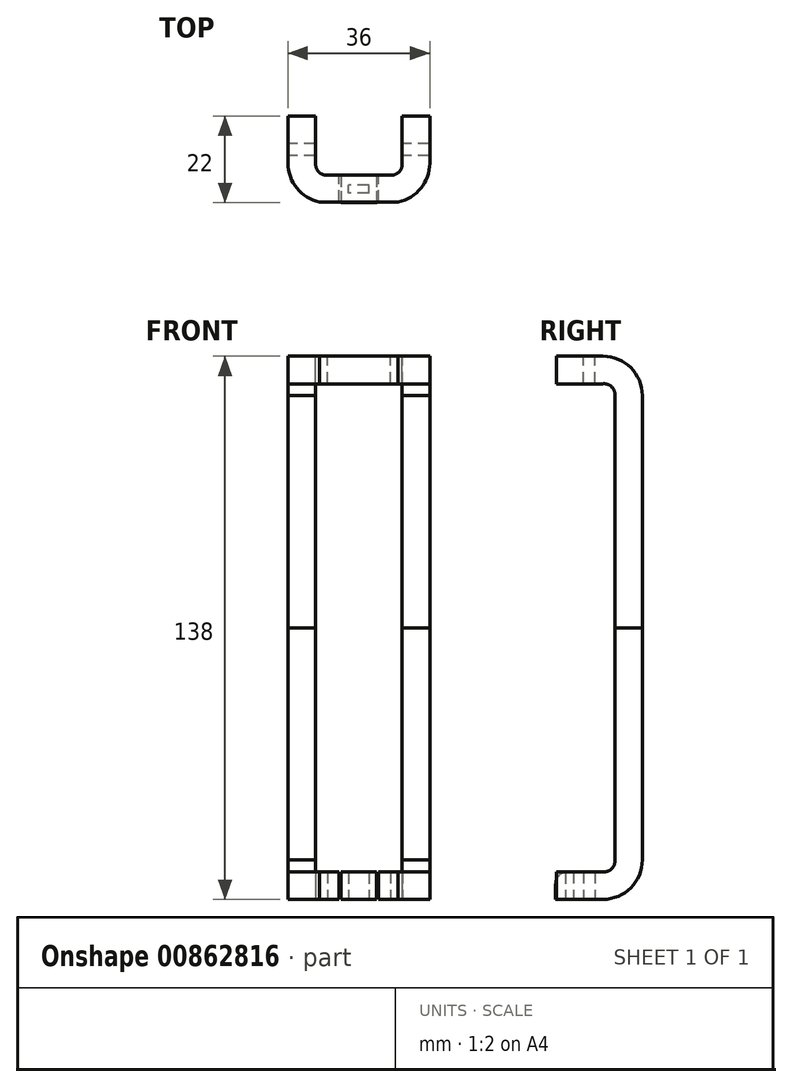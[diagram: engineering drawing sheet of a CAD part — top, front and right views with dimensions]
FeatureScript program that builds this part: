
annotation { "Feature Type Name" : "Feature", "Feature Type Description" : "" }
export const myFeature = defineFeature(function(context is Context, id is Id, definition is map)
    precondition{}
    {
        {
            assignVariable(context, id + "F0", {"name" : "frame_width", "anyValue" : 7});
        }
        {
            assignVariable(context, id + "F1", {"name" : "phone_height", "anyValue" : 138});
        }
        {
            var Q0;
            Q0=qCreatedBy(makeId("Top.planeOp"),FACE);
            var sketch = newSketch(context, id + "F2", { "sketchPlane" : qUnion([Q0])});
            skLineSegment(sketch, "E0", {"start": v(-126.35, 500.54) * mm, "end": v(-119.35, 500.54) * mm, "construction": true});
            skLineSegment(sketch, "E1", {"start": v(-126.35, 500.54) * mm, "end": v(-126.35, 495.54) * mm});
            skLineSegment(sketch, "E2", {"start": v(-116.35, 485.54) * mm, "end": v(-113.35, 485.54) * mm});
            skLineSegment(sketch, "E3", {"start": v(-113.35, 485.54) * mm, "end": v(-108.35, 485.54) * mm, "construction": true});
            skPoint(sketch, "E4.visualSharp", {"position": v(-126.35, 485.54) * mm});
            skArc(sketch, "E4.filletArc", {"start": v(-126.35, 495.54) * mm, "mid": v(-123.42, 488.47) * mm, "end": v(-116.35, 485.54) * mm});
            skPoint(sketch, "E5.visualSharp", {"position": v(-65.23, 485.8) * mm});
            skLineSegment(sketch, "E6", {"start": v(-113.35, 485.54) * mm, "end": v(-113.35, 492.54) * mm});
            skLineSegment(sketch, "E7", {"start": v(-126.35, 495.54) * mm, "end": v(-119.35, 495.54) * mm, "construction": true});
            skLineSegment(sketch, "E8", {"start": v(-116.35, 485.54) * mm, "end": v(-116.35, 492.54) * mm, "construction": true});
            skArc(sketch, "E9", {"start": v(-119.35, 495.54) * mm, "mid": v(-118.53, 493.36) * mm, "end": v(-116.35, 492.54) * mm});
            skLineSegment(sketch, "E10", {"start": v(-116.35, 492.54) * mm, "end": v(-113.35, 492.54) * mm});
            skLineSegment(sketch, "E11", {"start": v(-119.35, 495.54) * mm, "end": v(-119.35, 500.54) * mm});
            skLineSegment(sketch, "E12", {"start": v(-113.35, 489.04) * mm, "end": v(-108.35, 489.04) * mm, "construction": true});
            skLineSegment(sketch, "E13", {"start": v(-108.35, 489.04) * mm, "end": v(-103.35, 489.04) * mm, "construction": true});
            skLineSegment(sketch, "E14", {"start": v(-108.35, 489.04) * mm, "end": v(-108.35, 479.6) * mm, "construction": true});
            skLineSegment(sketch, "E15", {"start": v(-108.35, 489.04) * mm, "end": v(-108.35, 497.32) * mm, "construction": true});
            skLineSegment(sketch, "E16.MirrorCS", {"start": v(-103.35, 485.54) * mm, "end": v(-108.35, 485.54) * mm, "construction": true});
            skLineSegment(sketch, "E17.MirrorCS", {"start": v(-103.35, 485.54) * mm, "end": v(-103.35, 492.54) * mm});
            skLineSegment(sketch, "E18.MirrorCS", {"start": v(-100.35, 485.54) * mm, "end": v(-103.35, 485.54) * mm});
            skLineSegment(sketch, "E19.MirrorCS", {"start": v(-100.35, 492.54) * mm, "end": v(-103.35, 492.54) * mm});
            skArc(sketch, "E20.MirrorCS", {"start": v(-97.35, 495.54) * mm, "mid": v(-98.16, 493.36) * mm, "end": v(-100.35, 492.54) * mm});
            skArc(sketch, "E21.MirrorCS", {"start": v(-90.35, 495.54) * mm, "mid": v(-93.28, 488.47) * mm, "end": v(-100.35, 485.54) * mm});
            skLineSegment(sketch, "E22.MirrorCS", {"start": v(-90.35, 495.54) * mm, "end": v(-97.35, 495.54) * mm, "construction": true});
            skLineSegment(sketch, "E23.MirrorCS", {"start": v(-97.35, 495.54) * mm, "end": v(-97.35, 500.54) * mm});
            skLineSegment(sketch, "E24.MirrorCS", {"start": v(-90.35, 500.54) * mm, "end": v(-97.35, 500.54) * mm, "construction": true});
            skLineSegment(sketch, "E25.MirrorCS", {"start": v(-90.35, 500.54) * mm, "end": v(-90.35, 495.54) * mm});
            skLineSegment(sketch, "E26", {"start": v(-119.35, 500.54) * mm, "end": v(-119.35, 507.54) * mm});
            skLineSegment(sketch, "E27", {"start": v(-126.35, 500.54) * mm, "end": v(-126.35, 507.54) * mm});
            skLineSegment(sketch, "E28", {"start": v(-126.35, 507.54) * mm, "end": v(-119.35, 507.54) * mm});
            skLineSegment(sketch, "E29.MirrorCS", {"start": v(-97.35, 500.54) * mm, "end": v(-97.35, 507.54) * mm});
            skLineSegment(sketch, "E30.MirrorCS", {"start": v(-90.35, 500.54) * mm, "end": v(-90.35, 507.54) * mm});
            skLineSegment(sketch, "E31.MirrorCS", {"start": v(-90.35, 507.54) * mm, "end": v(-97.35, 507.54) * mm});
            skLineSegment(sketch, "E32", {"start": v(-112.85, 492.54) * mm, "end": v(-112.85, 485.54) * mm, "construction": true});
            skLineSegment(sketch, "E33", {"start": v(-103.85, 492.54) * mm, "end": v(-103.85, 485.54) * mm, "construction": true});
            skLineSegment(sketch, "E34", {"start": v(-113.35, 492.54) * mm, "end": v(-112.85, 492.54) * mm, "construction": true});
            skLineSegment(sketch, "E35", {"start": v(-99.12, 492.54) * mm, "end": v(-112.85, 492.54) * mm, "construction": true});
            skLineSegment(sketch, "E36", {"start": v(-103.35, 492.54) * mm, "end": v(-103.85, 492.54) * mm, "construction": true});
            skLineSegment(sketch, "E37", {"start": v(-103.85, 492.54) * mm, "end": v(-99.12, 492.54) * mm, "construction": true});
            skSolve(sketch);
        }
        {
            var Q0;
            Q0=makeQuery(id+"F2.imprint","IMPRINT",FACE,{"disambiguationData":[TD([[makeQuery(id+"F2.imprint","IMPRINT",EDGE,{"derivedFrom":sQuery(id+"F2.wireOp",EDGE,"E1")}),1.0]])]});
            var Q1;
            Q1=makeQuery(id+"F2.imprint","IMPRINT",FACE,{"disambiguationData":[TD([[makeQuery(id+"F2.imprint","IMPRINT",EDGE,{"derivedFrom":sQuery(id+"F2.wireOp",EDGE,"E17.MirrorCS")}),-1.0]])]});
            extrude(context, id + "F3", {"entities" : qUnion([Q0, Q1]), "depth" : (getVariable(context, 'phone_height')) / 2 * mm, "offsetDistance" : 25 * mm});
        }
        {
            var Q0;
            Q0=makeQuery(id+"F3.opExtrude","SWEPT_FACE",FACE,{"disambiguationData":[OSD([sQuery(id+"F2.wireOp",EDGE,"E1"),sQuery(id+"F2.wireOp",EDGE,"E27")])]});
            var sketch = newSketch(context, id + "F4", { "sketchPlane" : qUnion([Q0])});
            skLineSegment(sketch, "E38", {"start": v(-507.54, 69) * mm, "end": v(-485.74, 69) * mm});
            skLineSegment(sketch, "E39", {"start": v(-485.74, 0) * mm, "end": v(-485.74, 7) * mm});
            skLineSegment(sketch, "E40", {"start": v(-507.54, 10) * mm, "end": v(-507.54, 16.46) * mm});
            skLineSegment(sketch, "E41", {"start": v(-497.54, 0) * mm, "end": v(-485.74, 0) * mm});
            skLineSegment(sketch, "E42", {"start": v(-507.54, 16.46) * mm, "end": v(-507.54, 69) * mm});
            skLineSegment(sketch, "E43", {"start": v(-507.54, 69) * mm, "end": v(-500.57, 69) * mm});
            skLineSegment(sketch, "E44", {"start": v(-500.57, 69) * mm, "end": v(-500.57, 7.1) * mm});
            skLineSegment(sketch, "E45", {"start": v(-507.54, 0) * mm, "end": v(-507.54, 0) * mm});
            skPoint(sketch, "E46", {"position": v(-495.54, 7) * mm});
            skLineSegment(sketch, "E47", {"start": v(-500.54, 7) * mm, "end": v(-500.57, 12) * mm, "construction": true});
            skLineSegment(sketch, "E48", {"start": v(-500.54, 7) * mm, "end": v(-495.54, 7) * mm, "construction": true});
            skLineSegment(sketch, "E49", {"start": v(-485.74, 7) * mm, "end": v(-495.54, 7) * mm});
            skPoint(sketch, "E50.visualSharp", {"position": v(-507.54, 0) * mm});
            skArc(sketch, "E50.filletArc", {"start": v(-507.54, 10) * mm, "mid": v(-504.61, 2.93) * mm, "end": v(-497.54, 0) * mm});
            skPoint(sketch, "E51.endSnap0", {"position": v(-498.04, 7) * mm});
            skLineSegment(sketch, "E52", {"start": v(-507.54, 10) * mm, "end": v(-500.56, 10) * mm});
            skArc(sketch, "E53", {"start": v(-500.56, 10) * mm, "mid": v(-499.76, 7.79) * mm, "end": v(-497.54, 7) * mm});
            skLineSegment(sketch, "E54", {"start": v(-495.54, 7) * mm, "end": v(-497.54, 7) * mm});
            skSolve(sketch);
        }
        {
            var Q0;
            {var subQ8=sQuery(id+"F4.wireOp",EDGE,"E40");Q0=makeQuery(id+"F4.imprint","IMPRINT",FACE,{"disambiguationData":[TD([[makeQuery(id+"F4.imprint","IMPRINT",EDGE,{"derivedFrom":subQ8}),1.0]])]});}
            var Q1;
            {var subQ0=sQuery(id+"F4.wireOp",EDGE,"E39");Q1=makeQuery(id+"F4.imprint","IMPRINT",FACE,{"disambiguationData":[TD([[makeQuery(id+"F4.imprint","IMPRINT",EDGE,{"derivedFrom":subQ0}),1.0]])]});}
            var Q2;
            {var subQ3=sQuery(id+"F4.wireOp",EDGE,"E50.filletArc");Q2=makeQuery(id+"F4.imprint","IMPRINT",FACE,{"disambiguationData":[TD([[makeQuery(id+"F4.imprint","IMPRINT",EDGE,{"derivedFrom":subQ3}),1.0]])]});}
            extrude(context, id + "F5", {"entities" : qUnion([Q0, Q1, Q2]), "operationType" : NewBodyOperationType.INTERSECT, "oppositeDirection" : true, "depth" : 81.7 * mm, "offsetDistance" : 25 * mm});
        }
        {
            var Q0;
            Q0=makeQuery(id+"F3.opExtrude","SWEPT_BODY",BODY,{"disambiguationData":[OSD([sQuery(id+"F2.wireOp",EDGE,"E1"),sQuery(id+"F2.wireOp",EDGE,"E2"),sQuery(id+"F2.wireOp",EDGE,"E3"),sQuery(id+"F2.wireOp",EDGE,"E4.filletArc"),sQuery(id+"F2.wireOp",EDGE,"obsk3g0P-nJtu-QT1G-FohG-gz7rWDq2pBs8"),sQuery(id+"F2.wireOp",EDGE,"E9"),sQuery(id+"F2.wireOp",EDGE,"E10"),sQuery(id+"F2.wireOp",EDGE,"E11"),sQuery(id+"F2.wireOp",EDGE,"f647806e-f1ab-41c5-826c-117e73be01030.MirrorCS"),sQuery(id+"F2.wireOp",EDGE,"E16.MirrorCS"),sQuery(id+"F2.wireOp",EDGE,"E18.MirrorCS"),sQuery(id+"F2.wireOp",EDGE,"E19.MirrorCS"),sQuery(id+"F2.wireOp",EDGE,"E20.MirrorCS"),sQuery(id+"F2.wireOp",EDGE,"E21.MirrorCS"),sQuery(id+"F2.wireOp",EDGE,"E23.MirrorCS"),sQuery(id+"F2.wireOp",EDGE,"E25.MirrorCS"),sQuery(id+"F2.wireOp",EDGE,"E26"),sQuery(id+"F2.wireOp",EDGE,"E27"),sQuery(id+"F2.wireOp",EDGE,"E28"),sQuery(id+"F2.wireOp",EDGE,"E29.MirrorCS"),sQuery(id+"F2.wireOp",EDGE,"E30.MirrorCS"),sQuery(id+"F2.wireOp",EDGE,"E31.MirrorCS")])]});
            var Q1;
            {var subQ0=sQuery(id+"F2.wireOp",EDGE,"E27");var subQ1=sQuery(id+"F2.wireOp",EDGE,"E1");var subQ2=sQuery(id+"F2.wireOp",EDGE,"E26");var subQ3=sQuery(id+"F2.wireOp",EDGE,"E11");var subQ4=sQuery(id+"F2.wireOp",EDGE,"E28");Q1=makeQuery(id+"F5.boolean.opBoolean","SPLIT",FACE,{"disambiguationData":[TD([makeQuery(id+"F3.opExtrude","SWEPT_FACE",FACE,{"disambiguationData":[OSD([subQ4])]})])],"derivedFrom":makeQuery(id+"F3.opExtrude","CAP_FACE",FACE,{"disambiguationData":[OSD([subQ1,sQuery(id+"F2.wireOp",EDGE,"E2"),sQuery(id+"F2.wireOp",EDGE,"E3"),sQuery(id+"F2.wireOp",EDGE,"E4.filletArc"),sQuery(id+"F2.wireOp",EDGE,"obsk3g0P-nJtu-QT1G-FohG-gz7rWDq2pBs8"),sQuery(id+"F2.wireOp",EDGE,"E9"),sQuery(id+"F2.wireOp",EDGE,"E10"),subQ3,sQuery(id+"F2.wireOp",EDGE,"f647806e-f1ab-41c5-826c-117e73be01030.MirrorCS"),sQuery(id+"F2.wireOp",EDGE,"E16.MirrorCS"),sQuery(id+"F2.wireOp",EDGE,"E18.MirrorCS"),sQuery(id+"F2.wireOp",EDGE,"E19.MirrorCS"),sQuery(id+"F2.wireOp",EDGE,"E20.MirrorCS"),sQuery(id+"F2.wireOp",EDGE,"E21.MirrorCS"),sQuery(id+"F2.wireOp",EDGE,"E23.MirrorCS"),sQuery(id+"F2.wireOp",EDGE,"E25.MirrorCS"),subQ2,subQ0,subQ4,sQuery(id+"F2.wireOp",EDGE,"E29.MirrorCS"),sQuery(id+"F2.wireOp",EDGE,"E30.MirrorCS"),sQuery(id+"F2.wireOp",EDGE,"E31.MirrorCS")])],"isStart":false})});}
            mirror(context, id + "F6", {"entities" : qUnion([Q0]), "mirrorPlane" : qUnion([Q1])});
        }
        {
            var Q0;
            Q0=qCreatedBy(makeId("Top.planeOp"),FACE);
            var sketch = newSketch(context, id + "F7", { "sketchPlane" : qUnion([Q0])});
            skLineSegment(sketch, "E55.0", {"start": v(-112.85, 492.54) * mm, "end": v(-112.85, 485.54) * mm, "construction": true});
            skLineSegment(sketch, "E56.0", {"start": v(-99.12, 492.54) * mm, "end": v(-112.85, 492.54) * mm, "construction": true});
            skLineSegment(sketch, "E57.0", {"start": v(-103.85, 492.54) * mm, "end": v(-99.12, 492.54) * mm, "construction": true});
            skLineSegment(sketch, "E58.0", {"start": v(-103.85, 492.54) * mm, "end": v(-103.85, 485.54) * mm, "construction": true});
            skLineSegment(sketch, "E59.0", {"start": v(-103.35, 485.54) * mm, "end": v(-108.35, 485.54) * mm, "construction": true});
            skLineSegment(sketch, "E60.0", {"start": v(-113.35, 485.54) * mm, "end": v(-108.35, 485.54) * mm, "construction": true});
            skLineSegment(sketch, "E61.0", {"start": v(-108.35, 489.04) * mm, "end": v(-108.35, 479.6) * mm, "construction": true});
            skLineSegment(sketch, "E62.0", {"start": v(-108.35, 489.04) * mm, "end": v(-103.35, 489.04) * mm, "construction": true});
            skLineSegment(sketch, "E63.0", {"start": v(-113.35, 489.04) * mm, "end": v(-108.35, 489.04) * mm, "construction": true});
            skLineSegment(sketch, "E64.0", {"start": v(-108.35, 489.04) * mm, "end": v(-108.35, 497.32) * mm, "construction": true});
            skLineSegment(sketch, "E65.bottom", {"start": v(-112.85, 492.54) * mm, "end": v(-103.85, 492.54) * mm});
            skLineSegment(sketch, "E65.top", {"start": v(-112.85, 485.54) * mm, "end": v(-103.85, 485.54) * mm});
            skLineSegment(sketch, "E65.left", {"start": v(-112.85, 492.54) * mm, "end": v(-112.85, 485.54) * mm});
            skLineSegment(sketch, "E65.right", {"start": v(-103.85, 492.54) * mm, "end": v(-103.85, 485.54) * mm});
            skLineSegment(sketch, "E66.bottom", {"start": v(-105.73, 488.05) * mm, "end": v(-110.96, 488.05) * mm});
            skLineSegment(sketch, "E66.top", {"start": v(-105.73, 490.03) * mm, "end": v(-110.96, 490.03) * mm});
            skLineSegment(sketch, "E66.left", {"start": v(-105.73, 488.05) * mm, "end": v(-105.73, 490.03) * mm});
            skLineSegment(sketch, "E66.right", {"start": v(-110.96, 488.05) * mm, "end": v(-110.96, 490.03) * mm});
            skPoint(sketch, "E66.middle", {"position": v(-108.35, 489.04) * mm});
            skSolve(sketch);
        }
        {
            var Q0;
            Q0=makeQuery(id+"F7.imprint","IMPRINT",FACE,{"disambiguationData":[TD([[makeQuery(id+"F7.imprint","IMPRINT",EDGE,{"derivedFrom":sQuery(id+"F7.wireOp",EDGE,"E65.bottom")}),-1.0]])]});
            extrude(context, id + "F8", {"entities" : qUnion([Q0]), "depth" : (getVariable(context, 'frame_width')) * mm, "offsetDistance" : 25 * mm});
        }
        {
            var Q0;
            {var subQ0=sQuery(id+"F4.wireOp",EDGE,"E49");var subQ1=sQuery(id+"F4.wireOp",EDGE,"E39");Q0=makeQuery(id+"F5.boolean.opBoolean","COPY",EDGE,{"disambiguationData":[TD([makeQuery(id+"F3.opExtrude","SWEPT_FACE",FACE,{"disambiguationData":[OSD([sQuery(id+"F2.wireOp",EDGE,"E4.filletArc")])]})])],"derivedFrom":makeQuery(id+"F5.boolean.toolComplement.opBoolean","COPY",EDGE,{"derivedFrom":makeQuery(id+"F5.opExtrude","SWEPT_EDGE",EDGE,{"disambiguationData":[OSD([subQ1,subQ0])]})})});}
            var Q1;
            Q1=makeQuery(id+"F8.opExtrude","CAP_EDGE",EDGE,{"disambiguationData":[OSD([sQuery(id+"F7.wireOp",EDGE,"E65.top")])],"isStart":false});
            var Q2;
            {var subQ0=sQuery(id+"F4.wireOp",EDGE,"E49");var subQ1=sQuery(id+"F4.wireOp",EDGE,"E39");Q2=makeQuery(id+"F5.boolean.opBoolean","COPY",EDGE,{"disambiguationData":[TD([makeQuery(id+"F3.opExtrude","SWEPT_FACE",FACE,{"disambiguationData":[OSD([sQuery(id+"F2.wireOp",EDGE,"E17.MirrorCS")])]})])],"derivedFrom":makeQuery(id+"F5.boolean.toolComplement.opBoolean","COPY",EDGE,{"derivedFrom":makeQuery(id+"F5.opExtrude","SWEPT_EDGE",EDGE,{"disambiguationData":[OSD([subQ1,subQ0])]})})});}
            fillet(context, id + "F9", {"entities" : qUnion([Q0, Q1, Q2]), "radius" : 3 * mm, "tangentPropagation" : true, "allowEdgeOverflow" : false});
        }
        {
            var Q0;
            Q0=makeQuery(id+"F6.opPattern","COPY",FACE,{"derivedFrom":makeQuery(id+"F3.opExtrude","SWEPT_FACE",FACE,{"disambiguationData":[OSD([sQuery(id+"F2.wireOp",EDGE,"E17.MirrorCS")])]}),"instanceName":"1"});
            extrude(context, id + "F10", {"entities" : qUnion([Q0]), "operationType" : NewBodyOperationType.ADD, "depth" : 11.5 * mm, "offsetDistance" : 25 * mm});
        }
    });
